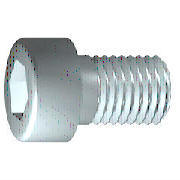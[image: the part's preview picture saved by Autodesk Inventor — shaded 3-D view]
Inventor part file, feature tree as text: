
AUTODESK INVENTOR PART (.ipt)
format: ipt  version: 2013 (Build 170138000, 138)  size: 182,784 bytes
history: native  units: mm (DEFAULTED — no unit token found)
features: sketch x2, extrude x1, plane x1, fillet x1
ambient origin geometry x7: Origin, YZ Plane, XY Plane, X Axis, Y Axis, Z Axis, Center Point
bodies: Solid1 (feature_tree), Body (feature_tree)
feature tree (5):
  extrude  "Slot"  Depth=0.306825mm
  plane  "Work Plane1"
  fillet  "Fillet2"  Radius=3.0mm
  sketch  "Sketch1"  dims[d1=18.0mm d2=0.306825mm d3=3.0mm]
  sketch  "Sketch2"  dims[d4=1.3mm d5=60.0deg d6=3.0mm d7=3.0mm d8=2.886751mm d9=5.5mm d10=90.0deg d11=10.0mm d12=0.0mm d13=18.0mm d14=0.0mm d15=0.306725mm d16=0.306725mm d17=0.3mm d19=0.0mm d26=25.0mm d27=45.0deg d28=0.0mm d29=0.0mm d30=0.1mm]
